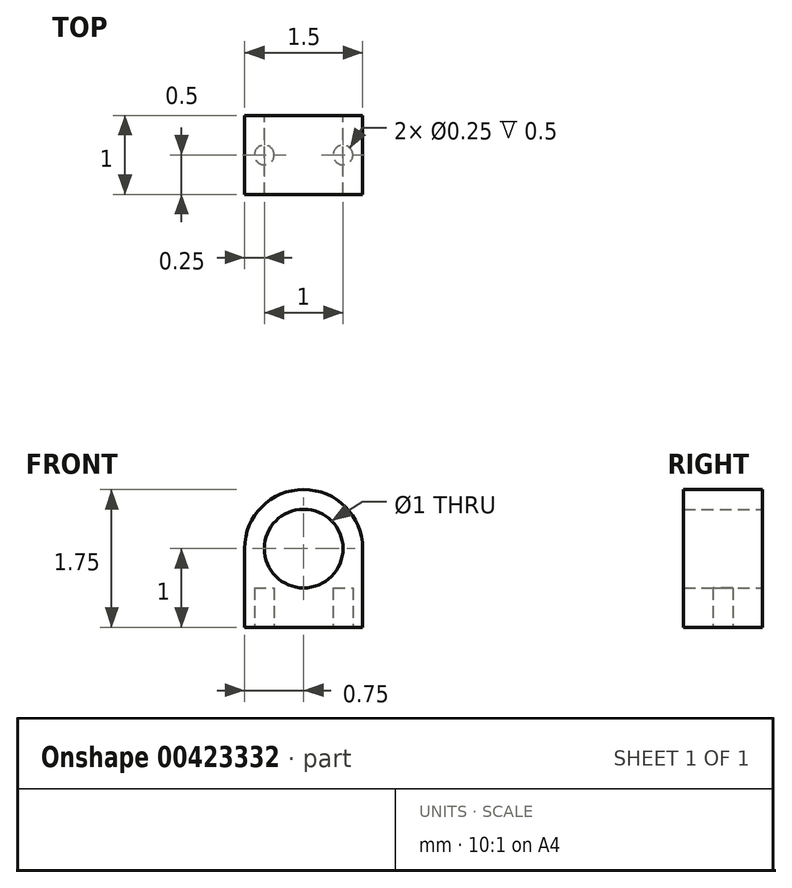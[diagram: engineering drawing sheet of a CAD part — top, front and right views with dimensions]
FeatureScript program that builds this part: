
annotation { "Feature Type Name" : "Feature", "Feature Type Description" : "" }
export const myFeature = defineFeature(function(context is Context, id is Id, definition is map)
    precondition{}
    {
        {
            var Q0;
            Q0=qCreatedBy(makeId("Front.planeOp"),FACE);
            var sketch = newSketch(context, id + "F0", { "sketchPlane" : qUnion([Q0])});
            skCircle(sketch, "E0", {"center": v(0, 0) * mm, "radius": 0.5 * mm});
            skArc(sketch, "E1", {"start": v(0.75, 0) * mm, "mid": v(0, 0.75) * mm, "end": v(-0.75, 0) * mm});
            skLineSegment(sketch, "E2.top", {"start": v(-0.75, -1) * mm, "end": v(0.75, -1) * mm});
            skLineSegment(sketch, "E2.left", {"start": v(-0.75, 0) * mm, "end": v(-0.75, -1) * mm});
            skLineSegment(sketch, "E2.right", {"start": v(0.75, 0) * mm, "end": v(0.75, -1) * mm});
            skSolve(sketch);
        }
        {
            var Q0;
            Q0=makeQuery(id+"F0.imprint","IMPRINT",FACE,{"disambiguationData":[TD([[makeQuery(id+"F0.imprint","IMPRINT",EDGE,{"derivedFrom":sQuery(id+"F0.wireOp",EDGE,"E0")}),-1.0]])]});
            extrude(context, id + "F1", {"entities" : qUnion([Q0]), "depth" : 1 * mm});
        }
        {
            var Q0;
            Q0=makeQuery(id+"F1.opExtrude","SWEPT_FACE",FACE,{"disambiguationData":[OSD([sQuery(id+"F0.wireOp",EDGE,"E2.top")])]});
            var sketch = newSketch(context, id + "F2", { "sketchPlane" : qUnion([Q0])});
            skCircle(sketch, "E3", {"center": v(-0.5, 0.5) * mm, "radius": 0.12 * mm});
            skPoint(sketch, "E3.centerSnap0", {"position": v(-0.75, 0.5) * mm});
            skCircle(sketch, "E4", {"center": v(0.5, 0.5) * mm, "radius": 0.12 * mm});
            skSolve(sketch);
        }
        {
            var Q0;
            Q0 = qSketchRegion(id + "F2", true);
            extrude(context, id + "F3", {"entities" : qUnion([Q0]), "operationType" : NewBodyOperationType.REMOVE, "oppositeDirection" : true, "depth" : 0.5 * mm});
        }
    });
